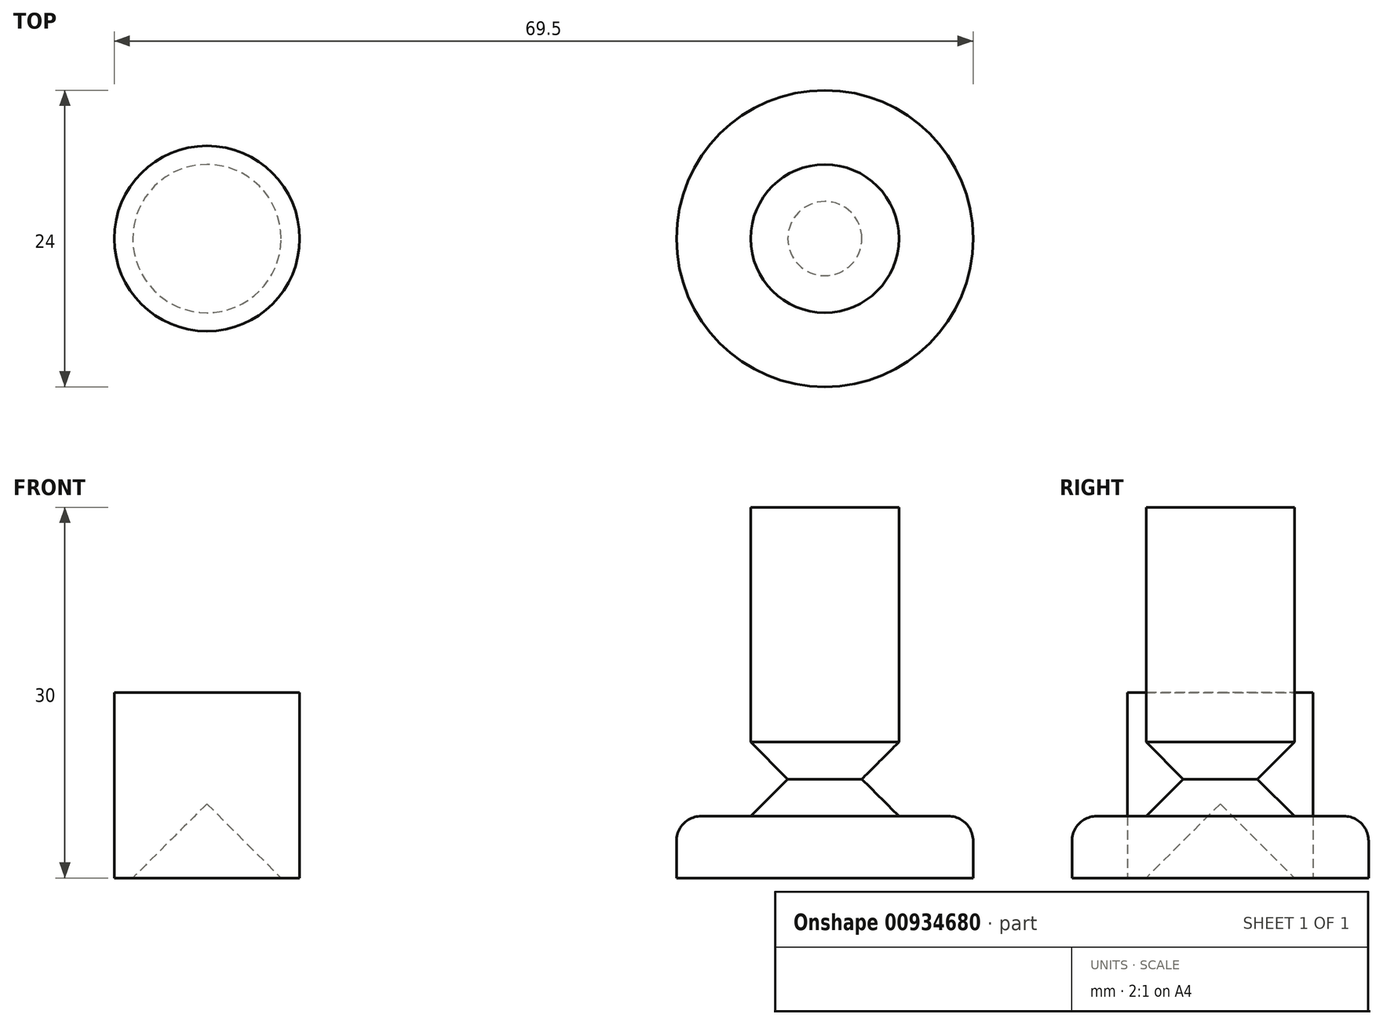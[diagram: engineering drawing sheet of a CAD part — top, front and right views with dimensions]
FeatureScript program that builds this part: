
annotation { "Feature Type Name" : "Feature", "Feature Type Description" : "" }
export const myFeature = defineFeature(function(context is Context, id is Id, definition is map)
    precondition{}
    {
        {
            var Q0;
            Q0=qCreatedBy(makeId("Top.planeOp"),FACE);
            var sketch = newSketch(context, id + "F0", { "sketchPlane" : qUnion([Q0])});
            skCircle(sketch, "E0", {"center": v(0, 0) * mm, "radius": 7.5 * mm});
            skSolve(sketch);
        }
        {
            var Q0;
            Q0=makeQuery(id+"F0.imprint","IMPRINT",FACE,{"disambiguationData":[TD([[makeQuery(id+"F0.imprint","IMPRINT",EDGE,{"derivedFrom":sQuery(id+"F0.wireOp",EDGE,"E0")}),1.0]])]});
            extrude(context, id + "F1", {"entities" : qUnion([Q0]), "depth" : 15 * mm, "offsetDistance" : 25 * mm});
        }
        {
            var Q0;
            Q0=qCreatedBy(makeId("Front.planeOp"),FACE);
            var sketch = newSketch(context, id + "F2", { "sketchPlane" : qUnion([Q0])});
            skLineSegment(sketch, "E1", {"start": v(0, 0) * mm, "end": v(6, 0) * mm});
            skLineSegment(sketch, "E2", {"start": v(6, 0) * mm, "end": v(0, 6) * mm});
            skLineSegment(sketch, "E3", {"start": v(0, 6) * mm, "end": v(0, 0) * mm});
            skSolve(sketch);
        }
        {
            var Q0;
            Q0 = qSketchRegion(id + "F2", true);
            var Q1;
            Q1=sQuery(id+"F2.wireOp",EDGE,"E3");
            revolve(context, id + "F3", {"operationType" : NewBodyOperationType.REMOVE, "surfaceOperationType" : NewSurfaceOperationType.NEW, "entities" : qUnion([Q0]), "axis" : qUnion([Q1]), "revolveType" : RevolveType.FULL, "oppositeDirection" : true});
        }
        {
            var Q0;
            Q0=qCreatedBy(makeId("Front.planeOp"),FACE);
            var sketch = newSketch(context, id + "F4", { "sketchPlane" : qUnion([Q0])});
            skLineSegment(sketch, "E4", {"start": v(0, 0) * mm, "end": v(12, 0) * mm});
            skLineSegment(sketch, "E5", {"start": v(12, 0) * mm, "end": v(12, 5) * mm});
            skLineSegment(sketch, "E6", {"start": v(12, 5) * mm, "end": v(6, 5) * mm});
            skLineSegment(sketch, "E7", {"start": v(6, 5) * mm, "end": v(3, 8) * mm});
            skLineSegment(sketch, "E8", {"start": v(3, 8) * mm, "end": v(6, 11) * mm});
            skLineSegment(sketch, "E9", {"start": v(6, 11) * mm, "end": v(6, 30) * mm});
            skLineSegment(sketch, "E10", {"start": v(6, 30) * mm, "end": v(0, 30) * mm});
            skLineSegment(sketch, "E11", {"start": v(0, 30) * mm, "end": v(0, 0) * mm});
            skLineSegment(sketch, "E12", {"start": v(6, 11) * mm, "end": v(6, 5) * mm, "construction": true});
            skSolve(sketch);
        }
        {
            var Q0;
            Q0=makeQuery(id+"F4.imprint","IMPRINT",FACE,{"disambiguationData":[TD([[makeQuery(id+"F4.imprint","IMPRINT",EDGE,{"derivedFrom":sQuery(id+"F4.wireOp",EDGE,"E4")}),1.0]])]});
            var Q1;
            Q1=sQuery(id+"F4.wireOp",EDGE,"E11");
            revolve(context, id + "F5", {"surfaceOperationType" : NewSurfaceOperationType.NEW, "entities" : qUnion([Q0]), "axis" : qUnion([Q1]), "revolveType" : RevolveType.FULL});
        }
        {
            var Q0;
            Q0=makeQuery(id+"F5.opRevolve","SWEPT_BODY",BODY,{"disambiguationData":[OSD([sQuery(id+"F4.wireOp",EDGE,"E4"),sQuery(id+"F4.wireOp",EDGE,"E5"),sQuery(id+"F4.wireOp",EDGE,"E6"),sQuery(id+"F4.wireOp",EDGE,"E7"),sQuery(id+"F4.wireOp",EDGE,"E8"),sQuery(id+"F4.wireOp",EDGE,"E9"),sQuery(id+"F4.wireOp",EDGE,"E10"),sQuery(id+"F4.wireOp",EDGE,"E11")])]});
            transform(context, id + "F6", {"entities" : qUnion([Q0]), "transformType" : TransformType.TRANSLATION_3D, "dx" : 50 * mm, "dy" : 0 * mm, "dz" : 0 * mm, "makeCopy" : false});
        }
        {
            var Q0;
            Q0=makeQuery(id+"F5.opRevolve","SWEPT_EDGE",EDGE,{"disambiguationData":[OSD([sQuery(id+"F4.wireOp",EDGE,"E5"),sQuery(id+"F4.wireOp",EDGE,"E6")])]});
            fillet(context, id + "F7", {"entities" : qUnion([Q0]), "radius" : 2 * mm, "tangentPropagation" : true, "allowEdgeOverflow" : false});
        }
    });
